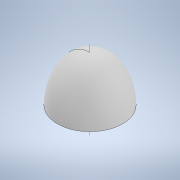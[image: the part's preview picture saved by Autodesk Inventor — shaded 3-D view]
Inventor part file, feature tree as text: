
AUTODESK INVENTOR PART (.ipt)
format: ipt  version: 2022 (Build 260153000, 153)  size: 337,920 bytes
history: native  units: in
note: dims shown in document units (in); Inventor stores cm internally (conversion verified against a paired STEP export)
features: sketch x3, revolve x1, thicken_offset x1, shell x1, extrude x1, other x1, helix x1
ambient origin geometry x8: Origin, YZ Plane, XZ Plane, XY Plane, X Axis, Y Axis, Z Axis, Center Point
bodies: Solid1 (feature_tree)
feature tree (9):
  revolve  "Revolution1"  [1 undecoded]
  thicken_offset  "Thicken1"
  shell  "Shell2"  Thickness=0.25in
  extrude  "Extrusion1"  Depth=2.2in
  sketch  "Sketch3"  dims[d18=0.125in d19=0.4in d20=0.3937in d21=0.0in d22=90.0deg d23=90.0deg d24=0.0in d25=0.0in d32=0.04in d33=0.09in d34=0.09in d35=60.0deg d4=0.0344in]
  other  "Work Axis1"
  helix  "Coil1"  [1 undecoded]
  sketch  "Sketch1"  dims[d3=90.0deg d5=0.26in d6=0.25in d7=0.25in]
  sketch  "Sketch2"  dims[d10=0.25in d11=0.0in d12=2.2in]
note: 2 required parameter values undecoded (feature->parameter linkage not recoverable at this tier; creation-order binding heuristic only, values carry confidence <= 0.55)